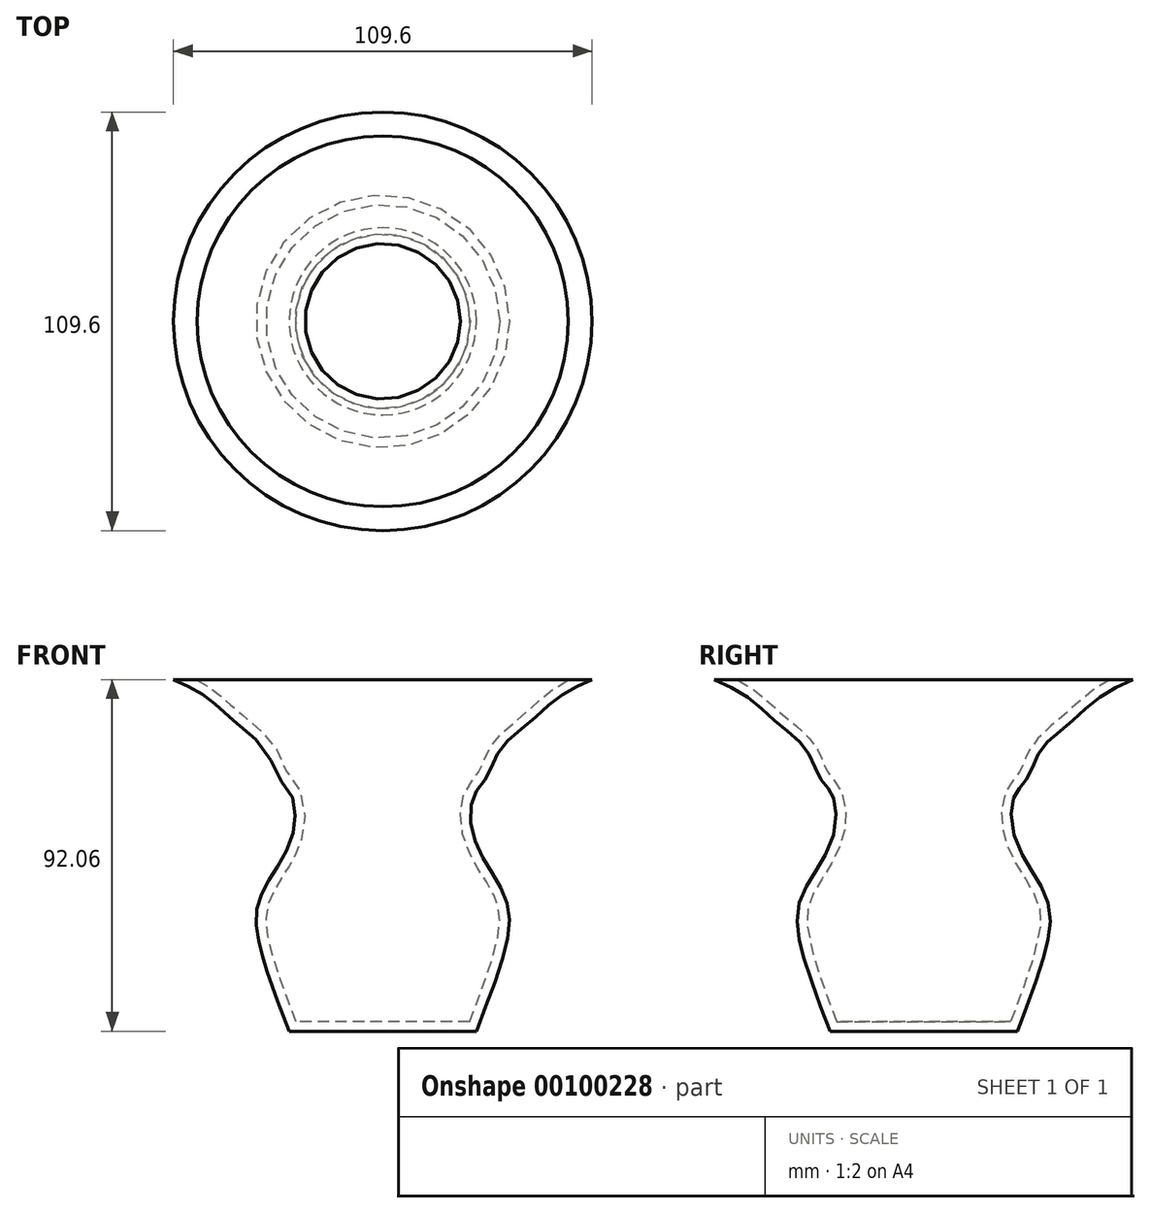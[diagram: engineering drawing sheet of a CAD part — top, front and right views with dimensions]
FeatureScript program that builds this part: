
annotation { "Feature Type Name" : "Feature", "Feature Type Description" : "" }
export const myFeature = defineFeature(function(context is Context, id is Id, definition is map)
    precondition{}
    {
        {
            var Q0;
            Q0=qCreatedBy(makeId("Front.planeOp"),FACE);
            var sketch = newSketch(context, id + "F0", { "sketchPlane" : qUnion([Q0])});
            skLineSegment(sketch, "E0", {"start": v(0, 97.24) * mm, "end": v(0, -94.45) * mm, "construction": true});
            skFitSpline(sketch, "E1", {"points": [v(24.5, 0) * mm, v(31.68, 20.32) * mm, v(32.88, 32.28) * mm, v(28.9, 41.05) * mm, v(23.71, 51.01) * mm, v(23.71, 61.37) * mm, v(27.3, 66.55) * mm, v(30.49, 73.33) * mm, v(38.46, 80.9) * mm, v(46.43, 87.67) * mm, v(54.8, 92.06) * mm], "startDerivative": vector(58.24, 150.46) * mm, "endDerivative": vector(91.9, 41.04) * mm});
            skLineSegment(sketch, "E2", {"start": v(24.5, 0) * mm, "end": v(0, 0) * mm});
            skLineSegment(sketch, "E3", {"start": v(54.8, 92.06) * mm, "end": v(0, 90.77) * mm});
            skLineSegment(sketch, "E4", {"start": v(0, 90.77) * mm, "end": v(0, 0) * mm});
            skSolve(sketch);
        }
        {
            var Q0;
            Q0=makeQuery(id+"F0.imprint","IMPRINT",FACE,{"disambiguationData":[TD([[makeQuery(id+"F0.imprint","IMPRINT",EDGE,{"derivedFrom":sQuery(id+"F0.wireOp",EDGE,"E1")}),1.0]])]});
            var Q1;
            Q1=sQuery(id+"F0.wireOp",EDGE,"E0");
            revolve(context, id + "F1", {"entities" : qUnion([Q0]), "axis" : qUnion([Q1]), "revolveType" : RevolveType.FULL});
        }
        {
            var Q0;
            Q0=makeQuery(id+"F1.opRevolve","SWEPT_FACE",FACE,{"disambiguationData":[OSD([sQuery(id+"F0.wireOp",EDGE,"E3")])]});
            shell(context, id + "F2", {"entities" : qUnion([Q0]), "thickness" : 2.54 * mm});
        }
    });
